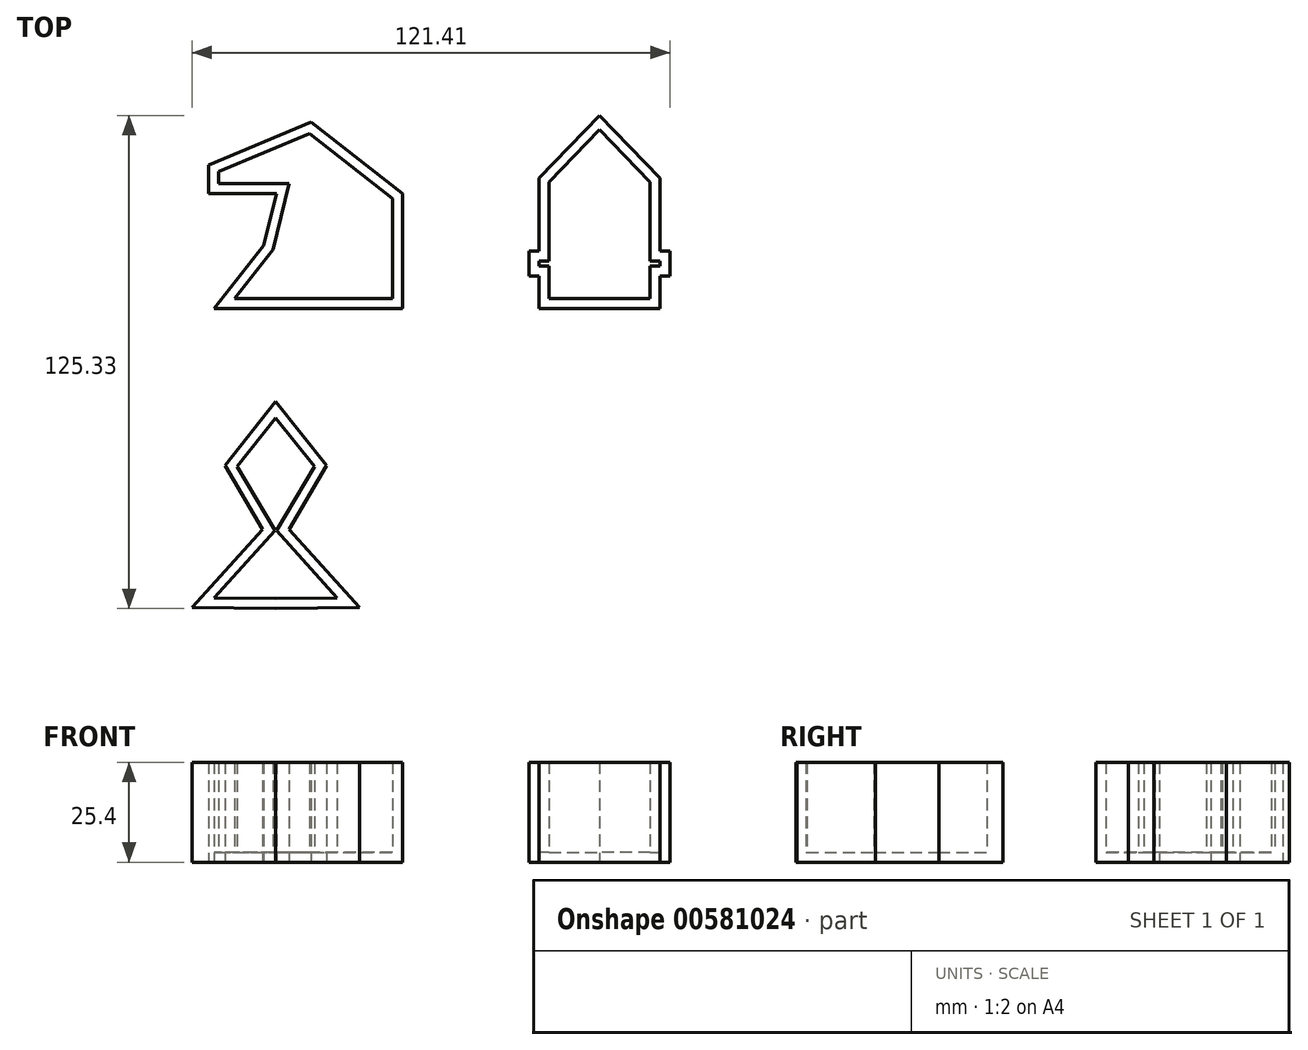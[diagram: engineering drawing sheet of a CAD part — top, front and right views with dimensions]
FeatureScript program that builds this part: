
annotation { "Feature Type Name" : "Feature", "Feature Type Description" : "" }
export const myFeature = defineFeature(function(context is Context, id is Id, definition is map)
    precondition{}
    {
        {
            var Q0;
            Q0=qCreatedBy(makeId("Top.planeOp"),FACE);
            var sketch = newSketch(context, id + "F0", { "sketchPlane" : qUnion([Q0])});
            skLineSegment(sketch, "E0", {"start": v(-57.49, 0) * mm, "end": v(-9.65, 0) * mm});
            skLineSegment(sketch, "E1", {"start": v(-9.65, 0) * mm, "end": v(-9.65, 29.23) * mm});
            skLineSegment(sketch, "E2", {"start": v(-9.65, 29.23) * mm, "end": v(-32.87, 47.42) * mm});
            skLineSegment(sketch, "E3", {"start": v(-32.87, 47.42) * mm, "end": v(-58.89, 36.5) * mm});
            skLineSegment(sketch, "E4", {"start": v(-58.89, 36.5) * mm, "end": v(-58.89, 29.23) * mm});
            skLineSegment(sketch, "E5", {"start": v(-58.89, 29.23) * mm, "end": v(-41.68, 29.23) * mm});
            skLineSegment(sketch, "E6", {"start": v(-41.68, 29.23) * mm, "end": v(-44.9, 16.09) * mm});
            skLineSegment(sketch, "E7", {"start": v(-44.9, 16.09) * mm, "end": v(-57.49, 0) * mm});
            skSolve(sketch);
        }
        {
            var Q0;
            Q0 = qSketchRegion(id + "F0", true);
            extrude(context, id + "F1", {"entities" : qUnion([Q0]), "depth" : 25.4 * mm, "offsetDistance" : 25.4 * mm});
        }
        {
            var Q0;
            Q0=makeQuery(id+"F1.opExtrude","CAP_FACE",FACE,{"disambiguationData":[OSD([sQuery(id+"F0.wireOp",EDGE,"E0"),sQuery(id+"F0.wireOp",EDGE,"E1"),sQuery(id+"F0.wireOp",EDGE,"E2"),sQuery(id+"F0.wireOp",EDGE,"E3"),sQuery(id+"F0.wireOp",EDGE,"E4"),sQuery(id+"F0.wireOp",EDGE,"E5"),sQuery(id+"F0.wireOp",EDGE,"E6"),sQuery(id+"F0.wireOp",EDGE,"E7")])],"isStart":false});
            shell(context, id + "F2", {"entities" : qUnion([Q0]), "thickness" : 2.54 * mm});
        }
        {
            var Q0;
            Q0=qCreatedBy(makeId("Top.planeOp"),FACE);
            var sketch = newSketch(context, id + "F3", { "sketchPlane" : qUnion([Q0])});
            skLineSegment(sketch, "E8", {"start": v(55.81, 0) * mm, "end": v(55.81, 8.25) * mm});
            skLineSegment(sketch, "E9", {"start": v(55.81, 8.25) * mm, "end": v(58.33, 8.25) * mm});
            skLineSegment(sketch, "E10", {"start": v(58.33, 8.25) * mm, "end": v(58.33, 14.69) * mm});
            skLineSegment(sketch, "E11", {"start": v(58.33, 14.69) * mm, "end": v(55.81, 14.69) * mm});
            skLineSegment(sketch, "E12", {"start": v(55.81, 14.69) * mm, "end": v(55.81, 33.15) * mm});
            skLineSegment(sketch, "E13", {"start": v(55.81, 33.15) * mm, "end": v(40.42, 49.1) * mm});
            skLineSegment(sketch, "E14", {"start": v(40.42, 0) * mm, "end": v(55.81, 0) * mm});
            skLineSegment(sketch, "E15.MirrorCS", {"start": v(40.42, 0) * mm, "end": v(25.04, 0) * mm});
            skLineSegment(sketch, "E16.MirrorCS", {"start": v(25.04, 0) * mm, "end": v(25.04, 8.25) * mm});
            skLineSegment(sketch, "E17.MirrorCS", {"start": v(22.52, 8.25) * mm, "end": v(22.52, 14.69) * mm});
            skLineSegment(sketch, "E18.MirrorCS", {"start": v(25.04, 14.69) * mm, "end": v(25.04, 33.15) * mm});
            skLineSegment(sketch, "E19.MirrorCS", {"start": v(25.04, 33.15) * mm, "end": v(40.42, 49.1) * mm});
            skLineSegment(sketch, "E20", {"start": v(25.04, 14.69) * mm, "end": v(22.52, 14.69) * mm});
            skLineSegment(sketch, "E21", {"start": v(25.04, 8.25) * mm, "end": v(22.52, 8.25) * mm});
            skSolve(sketch);
        }
        {
            var Q0;
            Q0 = qSketchRegion(id + "F3", true);
            extrude(context, id + "F4", {"entities" : qUnion([Q0]), "depth" : 25.4 * mm, "offsetDistance" : 25.4 * mm});
        }
        {
            var Q0;
            Q0=makeQuery(id+"F4.opExtrude","CAP_FACE",FACE,{"disambiguationData":[OSD([sQuery(id+"F3.wireOp",EDGE,"E8"),sQuery(id+"F3.wireOp",EDGE,"E9"),sQuery(id+"F3.wireOp",EDGE,"E10"),sQuery(id+"F3.wireOp",EDGE,"E11"),sQuery(id+"F3.wireOp",EDGE,"E12"),sQuery(id+"F3.wireOp",EDGE,"E13"),sQuery(id+"F3.wireOp",EDGE,"E14"),sQuery(id+"F3.wireOp",EDGE,"E15.MirrorCS"),sQuery(id+"F3.wireOp",EDGE,"E16.MirrorCS"),sQuery(id+"F3.wireOp",EDGE,"E17.MirrorCS"),sQuery(id+"F3.wireOp",EDGE,"E18.MirrorCS"),sQuery(id+"F3.wireOp",EDGE,"E19.MirrorCS"),sQuery(id+"F3.wireOp",EDGE,"E20"),sQuery(id+"F3.wireOp",EDGE,"E21")])],"isStart":false});
            shell(context, id + "F5", {"entities" : qUnion([Q0]), "thickness" : 2.54 * mm});
        }
        {
            var Q0;
            Q0=qCreatedBy(makeId("Top.planeOp"),FACE);
            var sketch = newSketch(context, id + "F6", { "sketchPlane" : qUnion([Q0])});
            skLineSegment(sketch, "E22.MirrorCS", {"start": v(-54.7, -39.87) * mm, "end": v(-41.82, -23.64) * mm});
            skLineSegment(sketch, "E23.MirrorCS", {"start": v(-45.18, -56.1) * mm, "end": v(-54.7, -39.87) * mm});
            skLineSegment(sketch, "E24.MirrorCS", {"start": v(-63.08, -75.95) * mm, "end": v(-45.18, -56.1) * mm});
            skLineSegment(sketch, "E25.MirrorCS", {"start": v(-41.82, -76.23) * mm, "end": v(-63.08, -75.95) * mm});
            skPoint(sketch, "E26.end.orphan", {"position": v(-41.82, -75.95) * mm});
            skPoint(sketch, "E27.start.orphan", {"position": v(-23.64, -75.95) * mm});
            skLineSegment(sketch, "E28", {"start": v(-41.82, -75.95) * mm, "end": v(-41.82, -76.23) * mm});
            skLineSegment(sketch, "E29.MirrorCS", {"start": v(-28.95, -39.87) * mm, "end": v(-41.82, -23.64) * mm});
            skLineSegment(sketch, "E30.MirrorCS", {"start": v(-38.47, -56.1) * mm, "end": v(-28.95, -39.87) * mm});
            skLineSegment(sketch, "E31.MirrorCS", {"start": v(-20.56, -75.95) * mm, "end": v(-38.47, -56.1) * mm});
            skLineSegment(sketch, "E32.MirrorCS", {"start": v(-41.82, -76.23) * mm, "end": v(-20.56, -75.95) * mm});
            skSolve(sketch);
        }
        {
            var Q0;
            Q0 = qSketchRegion(id + "F6", true);
            extrude(context, id + "F7", {"entities" : qUnion([Q0]), "depth" : 25.4 * mm, "offsetDistance" : 25.4 * mm});
        }
        {
            var Q0;
            Q0=makeQuery(id+"F7.opExtrude","CAP_FACE",FACE,{"disambiguationData":[OSD([sQuery(id+"F6.wireOp",EDGE,"E22.MirrorCS"),sQuery(id+"F6.wireOp",EDGE,"E23.MirrorCS"),sQuery(id+"F6.wireOp",EDGE,"E24.MirrorCS"),sQuery(id+"F6.wireOp",EDGE,"E25.MirrorCS"),sQuery(id+"F6.wireOp",EDGE,"E29.MirrorCS"),sQuery(id+"F6.wireOp",EDGE,"E30.MirrorCS"),sQuery(id+"F6.wireOp",EDGE,"E31.MirrorCS"),sQuery(id+"F6.wireOp",EDGE,"E32.MirrorCS")])],"isStart":false});
            shell(context, id + "F8", {"entities" : qUnion([Q0]), "thickness" : 2.54 * mm});
        }
    });
